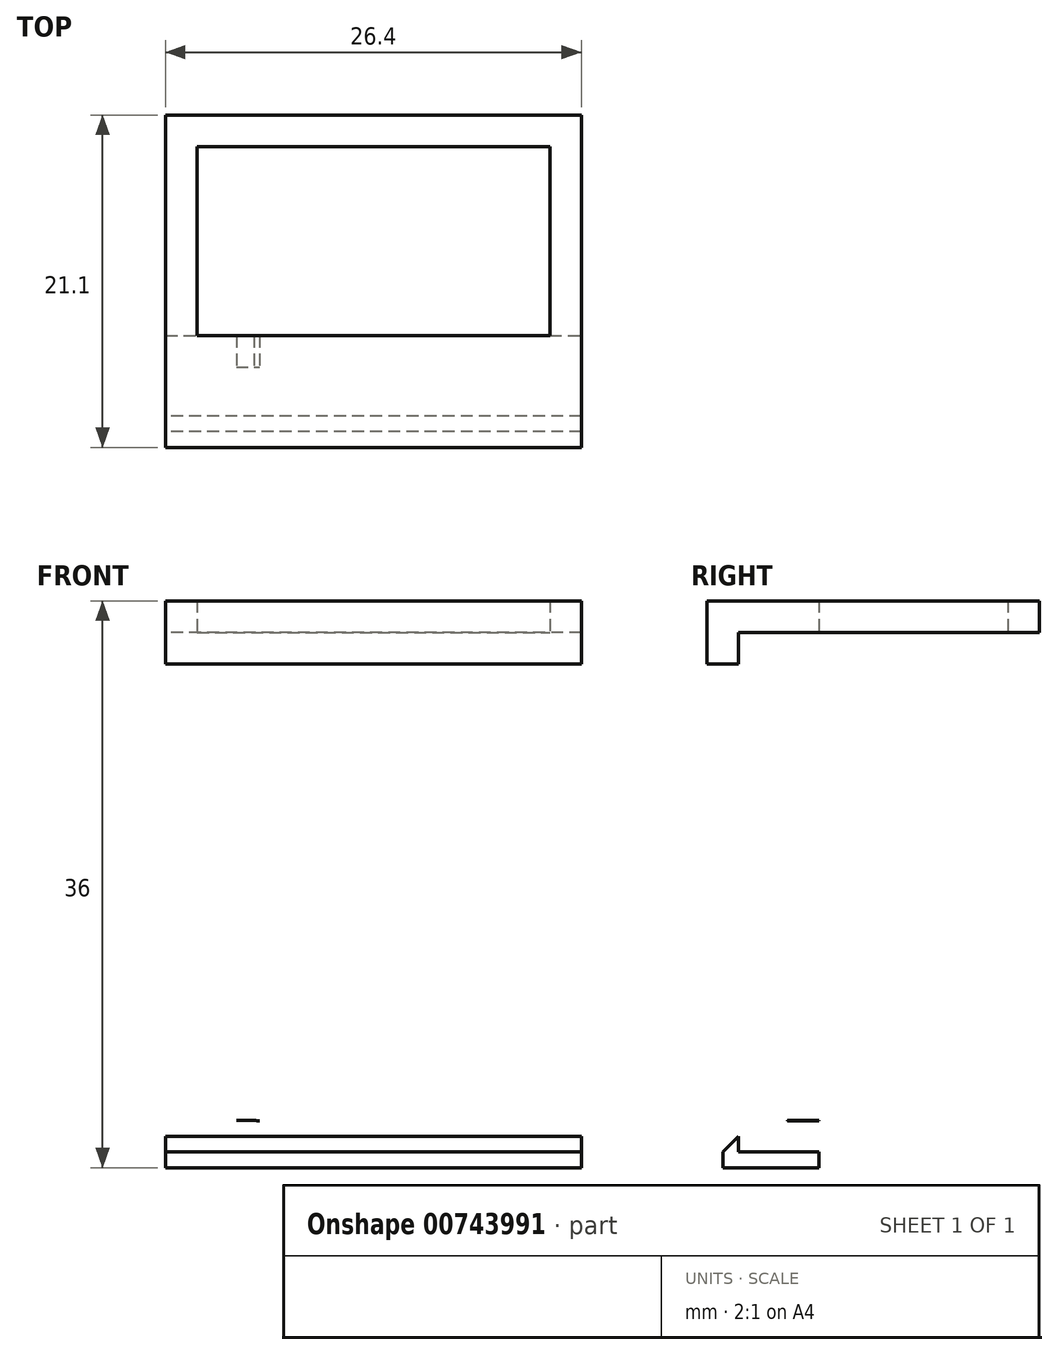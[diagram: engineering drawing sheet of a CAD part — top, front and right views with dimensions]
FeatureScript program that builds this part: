
annotation { "Feature Type Name" : "Feature", "Feature Type Description" : "" }
export const myFeature = defineFeature(function(context is Context, id is Id, definition is map)
    precondition{}
    {
        {
            var Q0;
            Q0=qCreatedBy(makeId("Top.planeOp"),FACE);
            var sketch = newSketch(context, id + "F0", { "sketchPlane" : qUnion([Q0])});
            skLineSegment(sketch, "E0", {"start": v(-21.57, 0) * mm, "end": v(29.71, 0) * mm, "construction": true});
            skLineSegment(sketch, "E1", {"start": v(0, 15.02) * mm, "end": v(0, -17.12) * mm, "construction": true});
            skLineSegment(sketch, "E2.bottom", {"start": v(-11.2, 6) * mm, "end": v(11.2, 6) * mm});
            skLineSegment(sketch, "E2.top", {"start": v(-11.2, -6) * mm, "end": v(11.2, -6) * mm});
            skLineSegment(sketch, "E2.left", {"start": v(-11.2, 6) * mm, "end": v(-11.2, -6) * mm});
            skLineSegment(sketch, "E2.right", {"start": v(11.2, 6) * mm, "end": v(11.2, -6) * mm});
            skLineSegment(sketch, "E3.0", {"start": v(-13.2, 8) * mm, "end": v(-13.2, -8) * mm});
            skLineSegment(sketch, "E3.1", {"start": v(-13.2, 8) * mm, "end": v(13.2, 8) * mm});
            skLineSegment(sketch, "E3.2", {"start": v(13.2, 8) * mm, "end": v(13.2, -8) * mm});
            skLineSegment(sketch, "E3.3", {"start": v(-13.2, -8) * mm, "end": v(13.2, -8) * mm});
            skSolve(sketch);
        }
        {
            var Q0;
            Q0=makeQuery(id+"F0.imprint","IMPRINT",FACE,{"disambiguationData":[TD([[makeQuery(id+"F0.imprint","IMPRINT",EDGE,{"derivedFrom":sQuery(id+"F0.wireOp",EDGE,"E2.bottom")}),1.0]])]});
            extrude(context, id + "F1", {"entities" : qUnion([Q0]), "depth" : 5 * mm, "offsetDistance" : 25 * mm});
        }
        {
            var Q0;
            Q0=makeQuery(id+"F1.opExtrude","CAP_FACE",FACE,{"disambiguationData":[OSD([sQuery(id+"F0.wireOp",EDGE,"E2.bottom"),sQuery(id+"F0.wireOp",EDGE,"E2.top"),sQuery(id+"F0.wireOp",EDGE,"E2.left"),sQuery(id+"F0.wireOp",EDGE,"E2.right"),sQuery(id+"F0.wireOp",EDGE,"E3.0"),sQuery(id+"F0.wireOp",EDGE,"E3.1"),sQuery(id+"F0.wireOp",EDGE,"E3.2"),sQuery(id+"F0.wireOp",EDGE,"E3.3")])],"isStart":true});
            var sketch = newSketch(context, id + "F2", { "sketchPlane" : qUnion([Q0])});
            skLineSegment(sketch, "E4.bottom", {"start": v(-13.2, 8) * mm, "end": v(13.2, 8) * mm});
            skLineSegment(sketch, "E4.top", {"start": v(-13.2, 6) * mm, "end": v(13.2, 6) * mm});
            skLineSegment(sketch, "E4.left", {"start": v(-13.2, 8) * mm, "end": v(-13.2, 6) * mm});
            skLineSegment(sketch, "E4.right", {"start": v(13.2, 8) * mm, "end": v(13.2, 6) * mm});
            skSolve(sketch);
        }
        {
            var Q0;
            Q0=makeQuery(id+"F2.imprint","IMPRINT",FACE,{"disambiguationData":[TD([[makeQuery(id+"F2.imprint","IMPRINT",EDGE,{"derivedFrom":sQuery(id+"F2.wireOp",EDGE,"E4.bottom")}),-1.0]])]});
            extrude(context, id + "F3", {"entities" : qUnion([Q0]), "operationType" : NewBodyOperationType.ADD, "depth" : 32 * mm, "offsetDistance" : 25 * mm});
        }
        {
            var Q0;
            Q0=makeQuery(id+"F3.boolean.opBoolean","MERGE",FACE,{"derivedFrom":[makeQuery(id+"F1.opExtrude","SWEPT_FACE",FACE,{"disambiguationData":[OSD([sQuery(id+"F0.wireOp",EDGE,"E3.3")])]}),makeQuery(id+"F3.opExtrude","SWEPT_FACE",FACE,{"disambiguationData":[OSD([sQuery(id+"F2.wireOp",EDGE,"E4.bottom")])]})]});
            var sketch = newSketch(context, id + "F4", { "sketchPlane" : qUnion([Q0])});
            skLineSegment(sketch, "E5.bottom", {"start": v(13.2, 5) * mm, "end": v(-13.2, 5) * mm});
            skLineSegment(sketch, "E5.top", {"start": v(13.2, 3) * mm, "end": v(-13.2, 3) * mm});
            skLineSegment(sketch, "E5.left", {"start": v(13.2, 5) * mm, "end": v(13.2, 3) * mm});
            skLineSegment(sketch, "E5.right", {"start": v(-13.2, 5) * mm, "end": v(-13.2, 3) * mm});
            skLineSegment(sketch, "E6.bottom", {"start": v(13.2, -32) * mm, "end": v(-13.2, -32) * mm});
            skLineSegment(sketch, "E6.top", {"start": v(13.2, -30) * mm, "end": v(-13.2, -30) * mm});
            skLineSegment(sketch, "E6.left", {"start": v(13.2, -32) * mm, "end": v(13.2, -30) * mm});
            skLineSegment(sketch, "E6.right", {"start": v(-13.2, -32) * mm, "end": v(-13.2, -30) * mm});
            skLineSegment(sketch, "E7", {"start": v(0, 11.1) * mm, "end": v(0, -37.75) * mm, "construction": true});
            skLineSegment(sketch, "E8.top", {"start": v(-8.7, -28) * mm, "end": v(8.7, -28) * mm});
            skLineSegment(sketch, "E8.left", {"start": v(-10.2, -17.8) * mm, "end": v(-10.2, -25.5) * mm});
            skLineSegment(sketch, "E8.right", {"start": v(10.2, -17.8) * mm, "end": v(10.2, -25.5) * mm});
            skLineSegment(sketch, "E9", {"start": v(-22.4, -13.5) * mm, "end": v(22, -13.5) * mm, "construction": true});
            skArc(sketch, "E10", {"start": v(10.2, -17.8) * mm, "mid": v(0, -7.6) * mm, "end": v(-10.2, -17.8) * mm});
            skLineSegment(sketch, "E11", {"start": v(-10.2, -25.02) * mm, "end": v(-10.2, -25.5) * mm});
            skLineSegment(sketch, "E12", {"start": v(-8.7, -28) * mm, "end": v(-7.25, -28.02) * mm});
            skLineSegment(sketch, "E13", {"start": v(10.2, -25) * mm, "end": v(10.2, -25.5) * mm});
            skLineSegment(sketch, "E14", {"start": v(8.7, -28) * mm, "end": v(7.2, -28) * mm});
            skPoint(sketch, "E15.visualSharp", {"position": v(-10.2, -27.98) * mm});
            skArc(sketch, "E15.filletArc", {"start": v(-10.2, -25.02) * mm, "mid": v(-9.34, -27.13) * mm, "end": v(-7.25, -28.02) * mm});
            skPoint(sketch, "E16.visualSharp", {"position": v(10.2, -28) * mm});
            skArc(sketch, "E16.filletArc", {"start": v(7.2, -28) * mm, "mid": v(9.32, -27.12) * mm, "end": v(10.2, -25) * mm});
            skSolve(sketch);
        }
        {
            var Q0;
            Q0=makeQuery(id+"F4.imprint","IMPRINT",FACE,{"disambiguationData":[TD([[makeQuery(id+"F4.imprint","IMPRINT",EDGE,{"derivedFrom":sQuery(id+"F4.wireOp",EDGE,"E5.bottom")}),-1.0]])]});
            var Q1;
            Q1=makeQuery(id+"F4.imprint","IMPRINT",FACE,{"disambiguationData":[TD([[makeQuery(id+"F4.imprint","IMPRINT",EDGE,{"derivedFrom":sQuery(id+"F4.wireOp",EDGE,"E6.bottom")}),1.0]])]});
            extrude(context, id + "F5", {"entities" : qUnion([Q0, Q1]), "operationType" : NewBodyOperationType.ADD, "depth" : 5.1 * mm, "offsetDistance" : 25 * mm});
        }
        {
            var Q0;
            Q0=makeQuery(id+"F5.opExtrude","SWEPT_FACE",FACE,{"disambiguationData":[OSD([sQuery(id+"F4.wireOp",EDGE,"E5.top")])]});
            var sketch = newSketch(context, id + "F6", { "sketchPlane" : qUnion([Q0])});
            skLineSegment(sketch, "E17.bottom", {"start": v(13.2, 13.1) * mm, "end": v(-13.2, 13.1) * mm});
            skLineSegment(sketch, "E17.top", {"start": v(13.2, 11.1) * mm, "end": v(-13.2, 11.1) * mm});
            skLineSegment(sketch, "E17.left", {"start": v(13.2, 13.1) * mm, "end": v(13.2, 11.1) * mm});
            skLineSegment(sketch, "E17.right", {"start": v(-13.2, 13.1) * mm, "end": v(-13.2, 11.1) * mm});
            skSolve(sketch);
        }
        {
            var Q0;
            Q0 = qSketchRegion(id + "F6", true);
            extrude(context, id + "F7", {"entities" : qUnion([Q0]), "operationType" : NewBodyOperationType.ADD, "depth" : 2 * mm, "offsetDistance" : 25 * mm});
        }
        {
            var Q0;
            Q0=makeQuery(id+"F5.opExtrude","SWEPT_FACE",FACE,{"disambiguationData":[OSD([sQuery(id+"F4.wireOp",EDGE,"E6.top")])]});
            var sketch = newSketch(context, id + "F8", { "sketchPlane" : qUnion([Q0])});
            skLineSegment(sketch, "E18.bottom", {"start": v(-13.2, -13.1) * mm, "end": v(13.2, -13.1) * mm});
            skLineSegment(sketch, "E18.top", {"start": v(-13.2, -11.1) * mm, "end": v(13.2, -11.1) * mm});
            skLineSegment(sketch, "E18.left", {"start": v(-13.2, -13.1) * mm, "end": v(-13.2, -11.1) * mm});
            skLineSegment(sketch, "E18.right", {"start": v(13.2, -13.1) * mm, "end": v(13.2, -11.1) * mm});
            skSolve(sketch);
        }
        {
            var Q0;
            Q0=makeQuery(id+"F8.imprint","IMPRINT",FACE,{"disambiguationData":[TD([[makeQuery(id+"F8.imprint","IMPRINT",EDGE,{"derivedFrom":sQuery(id+"F8.wireOp",EDGE,"E18.bottom")}),-1.0]])]});
            extrude(context, id + "F9", {"entities" : qUnion([Q0]), "operationType" : NewBodyOperationType.ADD, "depth" : 1 * mm, "offsetDistance" : 25 * mm});
        }
        {
            var Q0;
            Q0=makeQuery(id+"F9.boolean.opBoolean","MERGE",FACE,{"derivedFrom":[makeQuery(id+"F7.boolean.opBoolean","MERGE",FACE,{"derivedFrom":[makeQuery(id+"F5.boolean.opBoolean","MERGE",FACE,{"derivedFrom":[makeQuery(id+"F3.boolean.opBoolean","MERGE",FACE,{"derivedFrom":[makeQuery(id+"F1.opExtrude","SWEPT_FACE",FACE,{"disambiguationData":[OSD([sQuery(id+"F0.wireOp",EDGE,"E3.0")])]}),makeQuery(id+"F3.opExtrude","SWEPT_FACE",FACE,{"disambiguationData":[OSD([sQuery(id+"F2.wireOp",EDGE,"E4.left")])]})]}),makeQuery(id+"F5.opExtrude","SWEPT_FACE",FACE,{"disambiguationData":[OSD([sQuery(id+"F4.wireOp",EDGE,"E5.right")])]}),makeQuery(id+"F5.opExtrude","SWEPT_FACE",FACE,{"disambiguationData":[OSD([sQuery(id+"F4.wireOp",EDGE,"E6.right")])]})]}),makeQuery(id+"F7.opExtrude","SWEPT_FACE",FACE,{"disambiguationData":[OSD([sQuery(id+"F6.wireOp",EDGE,"E17.right")])]})]}),makeQuery(id+"F9.opExtrude","SWEPT_FACE",FACE,{"disambiguationData":[OSD([sQuery(id+"F8.wireOp",EDGE,"E18.left")])]})]});
            var sketch = newSketch(context, id + "F10", { "sketchPlane" : qUnion([Q0])});
            skLineSegment(sketch, "E19", {"start": v(12.1, -30) * mm, "end": v(12.1, -31) * mm});
            skLineSegment(sketch, "E20", {"start": v(11.1, -29) * mm, "end": v(12.1, -30) * mm});
            skLineSegment(sketch, "E21", {"start": v(6, -31) * mm, "end": v(12.1, -31) * mm});
            skLineSegment(sketch, "E22.0", {"start": v(6, -32) * mm, "end": v(6, -31) * mm});
            skPoint(sketch, "E23.orphan", {"position": v(6, 0) * mm});
            skLineSegment(sketch, "E24.0", {"start": v(6, -32) * mm, "end": v(13.1, -32) * mm});
            skLineSegment(sketch, "E25.0", {"start": v(13.1, -29) * mm, "end": v(13.1, -32) * mm});
            skLineSegment(sketch, "E26.0", {"start": v(13.1, -29) * mm, "end": v(11.1, -29) * mm});
            skSolve(sketch);
        }
        {
            var Q0;
            Q0=makeQuery(id+"F10.imprint","IMPRINT",FACE,{"disambiguationData":[TD([[makeQuery(id+"F10.imprint","IMPRINT",EDGE,{"derivedFrom":sQuery(id+"F10.wireOp",EDGE,"E19")}),1.0]])]});
            extrude(context, id + "F11", {"entities" : qUnion([Q0]), "operationType" : NewBodyOperationType.REMOVE, "endBound" : BoundingType.THROUGH_ALL, "oppositeDirection" : true, "depth" : 25 * mm, "offsetDistance" : 25 * mm});
        }
        {
            var Q0;
            Q0=makeQuery(id+"F9.boolean.opBoolean","MERGE",FACE,{"derivedFrom":[makeQuery(id+"F7.boolean.opBoolean","MERGE",FACE,{"derivedFrom":[makeQuery(id+"F5.boolean.opBoolean","MERGE",FACE,{"derivedFrom":[makeQuery(id+"F3.boolean.opBoolean","MERGE",FACE,{"derivedFrom":[makeQuery(id+"F1.opExtrude","SWEPT_FACE",FACE,{"disambiguationData":[OSD([sQuery(id+"F0.wireOp",EDGE,"E3.0")])]}),makeQuery(id+"F3.opExtrude","SWEPT_FACE",FACE,{"disambiguationData":[OSD([sQuery(id+"F2.wireOp",EDGE,"E4.left")])]})]}),makeQuery(id+"F5.opExtrude","SWEPT_FACE",FACE,{"disambiguationData":[OSD([sQuery(id+"F4.wireOp",EDGE,"E5.right")])]}),makeQuery(id+"F5.opExtrude","SWEPT_FACE",FACE,{"disambiguationData":[OSD([sQuery(id+"F4.wireOp",EDGE,"E6.right")])]})]}),makeQuery(id+"F7.opExtrude","SWEPT_FACE",FACE,{"disambiguationData":[OSD([sQuery(id+"F6.wireOp",EDGE,"E17.right")])]})]}),makeQuery(id+"F9.opExtrude","SWEPT_FACE",FACE,{"disambiguationData":[OSD([sQuery(id+"F8.wireOp",EDGE,"E18.left")])]})]});
            var sketch = newSketch(context, id + "F12", { "sketchPlane" : qUnion([Q0])});
            skLineSegment(sketch, "E27", {"start": v(6, 0) * mm, "end": v(6, -7) * mm});
            skLineSegment(sketch, "E28", {"start": v(6, -7) * mm, "end": v(0, 0) * mm});
            skLineSegment(sketch, "E29", {"start": v(0, 0) * mm, "end": v(6, 0) * mm});
            skSolve(sketch);
        }
        {
            var Q0;
            Q0=makeQuery(id+"F12.imprint","IMPRINT",FACE,{"disambiguationData":[TD([[makeQuery(id+"F12.imprint","IMPRINT",EDGE,{"derivedFrom":sQuery(id+"F12.wireOp",EDGE,"E27")}),1.0]])]});
            var Q1;
            Q1=makeQuery(id+"F1.opExtrude","SWEPT_FACE",FACE,{"disambiguationData":[OSD([sQuery(id+"F0.wireOp",EDGE,"E2.left")])]});
            extrude(context, id + "F13", {"entities" : qUnion([Q0]), "operationType" : NewBodyOperationType.ADD, "endBound" : BoundingType.UP_TO_SURFACE, "oppositeDirection" : true, "depth" : 25 * mm, "endBoundEntityFace" : qUnion([Q1]), "offsetDistance" : 25 * mm});
        }
        {
            var Q0;
            Q0 = qSketchRegion(id + "F12", true);
            var Q1;
            Q1=makeQuery(id+"F9.boolean.opBoolean","MERGE",FACE,{"derivedFrom":[makeQuery(id+"F7.boolean.opBoolean","MERGE",FACE,{"derivedFrom":[makeQuery(id+"F5.boolean.opBoolean","MERGE",FACE,{"derivedFrom":[makeQuery(id+"F3.boolean.opBoolean","MERGE",FACE,{"derivedFrom":[makeQuery(id+"F1.opExtrude","SWEPT_FACE",FACE,{"disambiguationData":[OSD([sQuery(id+"F0.wireOp",EDGE,"E3.2")])]}),makeQuery(id+"F3.opExtrude","SWEPT_FACE",FACE,{"disambiguationData":[OSD([sQuery(id+"F2.wireOp",EDGE,"E4.right")])]})]}),makeQuery(id+"F5.opExtrude","SWEPT_FACE",FACE,{"disambiguationData":[OSD([sQuery(id+"F4.wireOp",EDGE,"E5.left")])]}),makeQuery(id+"F5.opExtrude","SWEPT_FACE",FACE,{"disambiguationData":[OSD([sQuery(id+"F4.wireOp",EDGE,"E6.left")])]})]}),makeQuery(id+"F7.opExtrude","SWEPT_FACE",FACE,{"disambiguationData":[OSD([sQuery(id+"F6.wireOp",EDGE,"E17.left")])]})]}),makeQuery(id+"F9.opExtrude","SWEPT_FACE",FACE,{"disambiguationData":[OSD([sQuery(id+"F8.wireOp",EDGE,"E18.right")])]})]});
            extrude(context, id + "F14", {"entities" : qUnion([Q0]), "operationType" : NewBodyOperationType.ADD, "endBound" : BoundingType.UP_TO_SURFACE, "oppositeDirection" : true, "depth" : 25 * mm, "endBoundEntityFace" : qUnion([Q1]), "offsetDistance" : 22 * mm});
        }
        {
            var Q0;
            Q0=makeQuery(id+"F14.opExtrude","SWEPT_FACE",FACE,{"disambiguationData":[OSD([sQuery(id+"F12.wireOp",EDGE,"E29")])]});
            extrude(context, id + "F15", {"entities" : qUnion([Q0]), "operationType" : NewBodyOperationType.REMOVE, "endBound" : BoundingType.THROUGH_ALL, "oppositeDirection" : true, "depth" : 25 * mm, "offsetDistance" : 25 * mm});
        }
        {
            var Q0;
            Q0=makeQuery(id+"F4.imprint","IMPRINT",FACE,{"disambiguationData":[TD([[makeQuery(id+"F4.imprint","IMPRINT",EDGE,{"derivedFrom":sQuery(id+"F4.wireOp",EDGE,"E8.top")}),1.0]])]});
            extrude(context, id + "F16", {"entities" : qUnion([Q0]), "operationType" : NewBodyOperationType.REMOVE, "oppositeDirection" : true, "depth" : 25 * mm, "offsetDistance" : 25 * mm});
        }
    });
